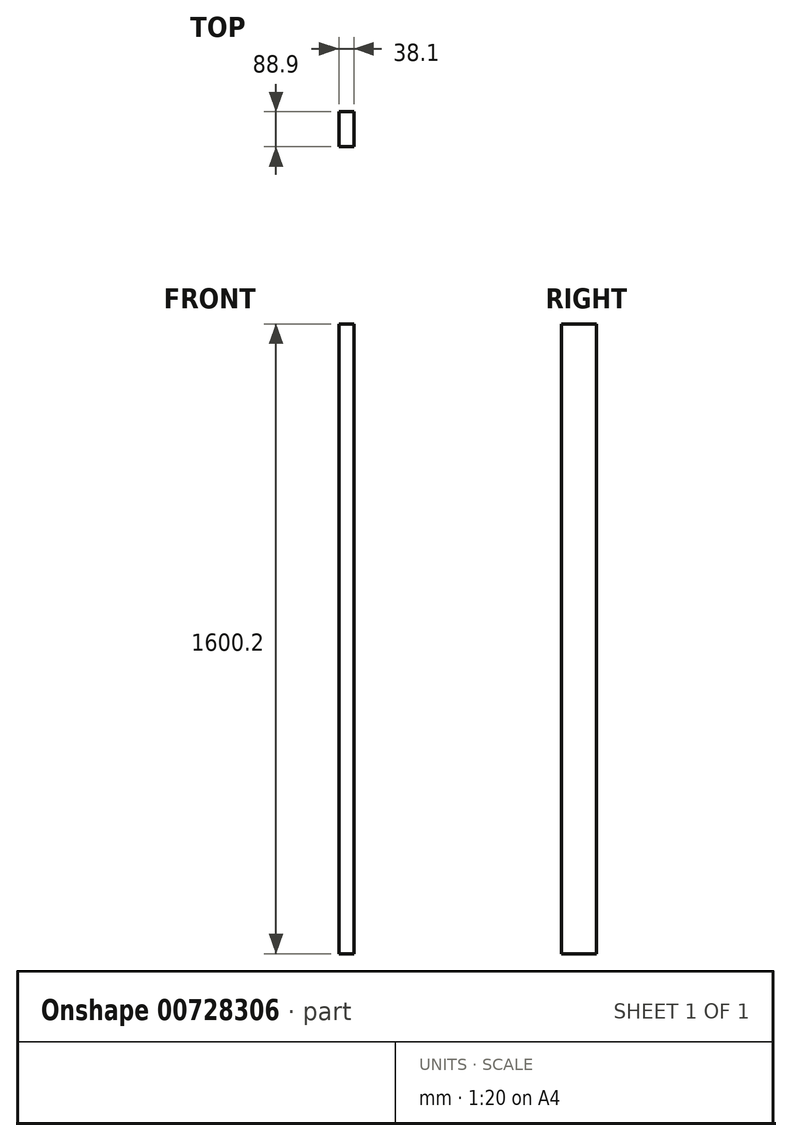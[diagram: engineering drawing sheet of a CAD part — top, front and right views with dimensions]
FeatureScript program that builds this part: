
annotation { "Feature Type Name" : "Feature", "Feature Type Description" : "" }
export const myFeature = defineFeature(function(context is Context, id is Id, definition is map)
    precondition{}
    {
        {
            var Q0;
            Q0=qCreatedBy(makeId("Front.planeOp"),FACE);
            var sketch = newSketch(context, id + "F0", { "sketchPlane" : qUnion([Q0])});
            skLineSegment(sketch, "E0.bottom", {"start": v(-19.05, -800.1) * mm, "end": v(19.05, -800.1) * mm});
            skLineSegment(sketch, "E0.top", {"start": v(-19.05, 800.1) * mm, "end": v(19.05, 800.1) * mm});
            skLineSegment(sketch, "E0.left", {"start": v(-19.05, -800.1) * mm, "end": v(-19.05, 800.1) * mm});
            skLineSegment(sketch, "E0.right", {"start": v(19.05, -800.1) * mm, "end": v(19.05, 800.1) * mm});
            skPoint(sketch, "E0.middle", {"position": v(0, 0) * mm});
            skSolve(sketch);
        }
        {
            var Q0;
            Q0=qSketchRegion(id+"F0",true);
            extrude(context, id + "F1", {"entities" : qUnion([Q0]), "depth" : 88.9 * mm, "offsetDistance" : 25.4 * mm});
        }
    });
